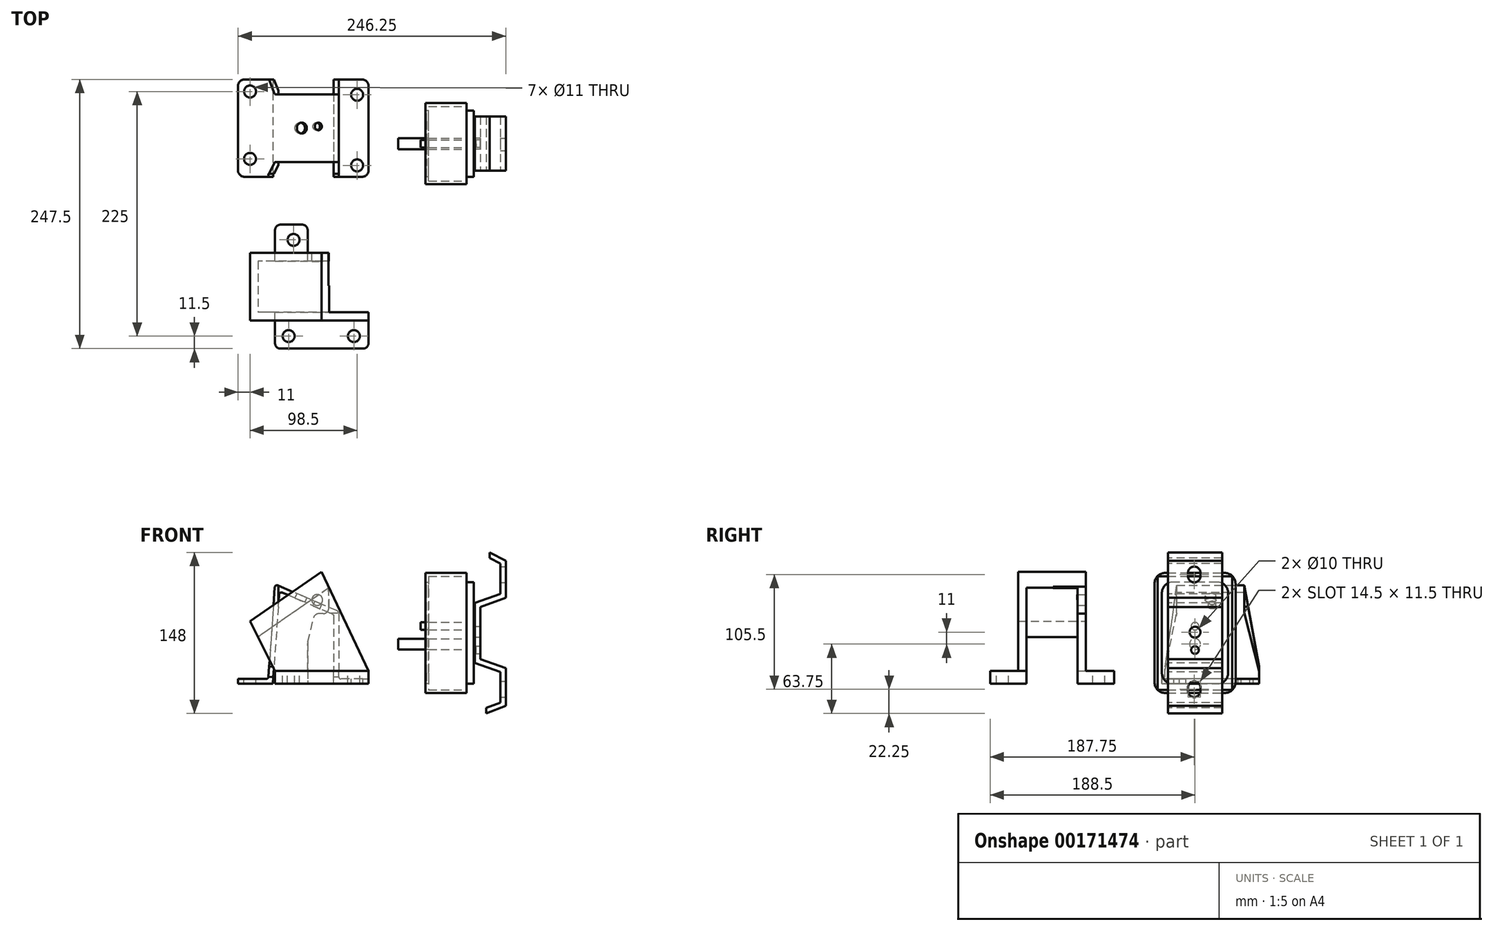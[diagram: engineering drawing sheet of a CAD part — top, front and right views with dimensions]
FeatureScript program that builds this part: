
annotation { "Feature Type Name" : "Feature", "Feature Type Description" : "" }
export const myFeature = defineFeature(function(context is Context, id is Id, definition is map)
    precondition{}
    {
        {
            var Q0;
            Q0=qCreatedBy(makeId("Front.planeOp"),FACE);
            var sketch = newSketch(context, id + "F0", { "sketchPlane" : qUnion([Q0])});
            skLineSegment(sketch, "E0", {"start": v(0, 0) * mm, "end": v(-120, 0) * mm});
            skPoint(sketch, "E1", {"position": v(-60, 0) * mm});
            skPoint(sketch, "E2", {"position": v(-32, 0) * mm});
            skPoint(sketch, "E3", {"position": v(-88, 0) * mm});
            skLineSegment(sketch, "E4", {"start": v(-32, 0) * mm, "end": v(-32, 63.5) * mm});
            skPoint(sketch, "E5", {"position": v(-82, 85) * mm});
            skLineSegment(sketch, "E6", {"start": v(-82, 85) * mm, "end": v(-88, 0) * mm});
            skLineSegment(sketch, "E7", {"start": v(-82, 85) * mm, "end": v(-32, 63.5) * mm});
            skLineSegment(sketch, "E8.0", {"start": v(-86.04, 91.64) * mm, "end": v(-92.49, 0.32) * mm});
            skLineSegment(sketch, "E8.1", {"start": v(-86.04, 91.64) * mm, "end": v(-27.5, 66.46) * mm});
            skLineSegment(sketch, "E8.2", {"start": v(-27.5, 0) * mm, "end": v(-27.5, 66.46) * mm});
            skLineSegment(sketch, "E9", {"start": v(-32, 0) * mm, "end": v(-27.5, 0) * mm});
            skPoint(sketch, "E10", {"position": v(-92.5, 0) * mm});
            skLineSegment(sketch, "E11", {"start": v(-92.5, 0) * mm, "end": v(-92.49, 0.32) * mm});
            skLineSegment(sketch, "E12", {"start": v(0, 0) * mm, "end": v(0, 4.5) * mm});
            skLineSegment(sketch, "E13", {"start": v(0, 4.5) * mm, "end": v(-27.5, 4.5) * mm});
            skLineSegment(sketch, "E14", {"start": v(-120, 0) * mm, "end": v(-120, 4.5) * mm});
            skLineSegment(sketch, "E15", {"start": v(-120, 4.5) * mm, "end": v(-92.2, 4.5) * mm});
            skSolve(sketch);
        }
        {
            var Q0;
            Q0=makeQuery(id+"F0.imprint","IMPRINT",FACE,{"disambiguationData":[TD([[makeQuery(id+"F0.imprint","IMPRINT",EDGE,{"derivedFrom":sQuery(id+"F0.wireOp",EDGE,"E4")}),-1.0]])]});
            var Q1;
            {var subQ0=sQuery(id+"F0.wireOp",EDGE,"E12");Q1=makeQuery(id+"F0.imprint","IMPRINT",FACE,{"disambiguationData":[TD([[makeQuery(id+"F0.imprint","IMPRINT",EDGE,{"derivedFrom":subQ0}),1.0]])]});}
            var Q2;
            {var subQ1=sQuery(id+"F0.wireOp",EDGE,"E11");Q2=makeQuery(id+"F0.imprint","IMPRINT",FACE,{"disambiguationData":[TD([[makeQuery(id+"F0.imprint","IMPRINT",EDGE,{"derivedFrom":subQ1}),1.0]])]});}
            extrude(context, id + "F1", {"entities" : qUnion([Q0, Q1, Q2]), "oppositeDirection" : true, "depth" : 89.5 * mm});
        }
        {
            var Q0;
            Q0=makeQuery(id+"F1.opExtrude","SWEPT_EDGE",EDGE,{"disambiguationData":[OSD([sQuery(id+"F0.wireOp",EDGE,"E8.0"),sQuery(id+"F0.wireOp",EDGE,"E8.1")])]});
            var Q1;
            Q1=makeQuery(id+"F1.opExtrude","SWEPT_EDGE",EDGE,{"disambiguationData":[OSD([sQuery(id+"F0.wireOp",EDGE,"E6"),sQuery(id+"F0.wireOp",EDGE,"E7")])]});
            var Q2;
            Q2=makeQuery(id+"F1.opExtrude","SWEPT_EDGE",EDGE,{"disambiguationData":[OSD([sQuery(id+"F0.wireOp",EDGE,"E4"),sQuery(id+"F0.wireOp",EDGE,"E7")])]});
            var Q3;
            Q3=makeQuery(id+"F1.opExtrude","SWEPT_EDGE",EDGE,{"disambiguationData":[OSD([sQuery(id+"F0.wireOp",EDGE,"E8.1"),sQuery(id+"F0.wireOp",EDGE,"E8.2")])]});
            var Q4;
            Q4=makeQuery(id+"F1.opExtrude","SWEPT_EDGE",EDGE,{"disambiguationData":[OSD([sQuery(id+"F0.wireOp",EDGE,"E8.0"),sQuery(id+"F0.wireOp",EDGE,"E15")])]});
            var Q5;
            Q5=makeQuery(id+"F1.opExtrude","SWEPT_EDGE",EDGE,{"disambiguationData":[OSD([sQuery(id+"F0.wireOp",EDGE,"E8.2"),sQuery(id+"F0.wireOp",EDGE,"E13")])]});
            fillet(context, id + "F2", {"entities" : qUnion([Q0, Q1, Q2, Q3, Q4, Q5]), "radius" : 2 * mm, "tangentPropagation" : true, "allowEdgeOverflow" : false});
        }
        {
            var Q0;
            Q0=makeQuery(id+"F1.opExtrude","SWEPT_FACE",FACE,{"disambiguationData":[OSD([sQuery(id+"F0.wireOp",EDGE,"E8.2")])]});
            var sketch = newSketch(context, id + "F3", { "sketchPlane" : qUnion([Q0])});
            skLineSegment(sketch, "E16.0", {"start": v(89.5, 90.52) * mm, "end": v(0, 90.52) * mm});
            skPoint(sketch, "E17", {"position": v(44.75, 90.52) * mm});
            skPoint(sketch, "E18", {"position": v(75.85, 90.52) * mm});
            skPoint(sketch, "E19", {"position": v(13.65, 90.52) * mm});
            skLineSegment(sketch, "E20.0", {"start": v(89.5, 65.15) * mm, "end": v(0, 65.15) * mm});
            skLineSegment(sketch, "E21.0", {"start": v(0, 6.5) * mm, "end": v(89.5, 6.5) * mm});
            skPoint(sketch, "E22", {"position": v(44.75, 6.5) * mm});
            skPoint(sketch, "E23", {"position": v(2.75, 6.5) * mm});
            skLineSegment(sketch, "E24", {"start": v(13.65, 90.52) * mm, "end": v(13.65, 65.15) * mm});
            skLineSegment(sketch, "E25", {"start": v(75.85, 90.52) * mm, "end": v(75.85, 65.15) * mm});
            skLineSegment(sketch, "E26.0", {"start": v(0, 6.5) * mm, "end": v(0, 65.15) * mm});
            skLineSegment(sketch, "E27.0", {"start": v(89.5, 6.5) * mm, "end": v(89.5, 65.15) * mm});
            skLineSegment(sketch, "E28.0", {"start": v(0, 90.52) * mm, "end": v(0, 66.98) * mm});
            skLineSegment(sketch, "E29.0", {"start": v(89.5, 90.52) * mm, "end": v(89.5, 66.98) * mm});
            skLineSegment(sketch, "E30", {"start": v(0, 66.98) * mm, "end": v(0, 65.15) * mm});
            skLineSegment(sketch, "E31", {"start": v(89.5, 66.98) * mm, "end": v(89.5, 65.15) * mm});
            skLineSegment(sketch, "E32", {"start": v(0, 90.52) * mm, "end": v(0, 93.52) * mm});
            skLineSegment(sketch, "E33", {"start": v(89.5, 6.5) * mm, "end": v(89.5, 11.5) * mm});
            skLineSegment(sketch, "E34", {"start": v(2.75, 6.5) * mm, "end": v(2.75, 11.5) * mm});
            skLineSegment(sketch, "E35", {"start": v(2.75, 11.5) * mm, "end": v(13.65, 65.15) * mm});
            skLineSegment(sketch, "E36", {"start": v(75.85, 65.15) * mm, "end": v(89.5, 11.5) * mm});
            skSolve(sketch);
        }
        {
            var Q0;
            {var subQ0=sQuery(id+"F3.wireOp",EDGE,"E25");Q0=makeQuery(id+"F3.imprint","IMPRINT",FACE,{"disambiguationData":[TD([[makeQuery(id+"F3.imprint","IMPRINT",EDGE,{"derivedFrom":subQ0}),1.0]])]});}
            var Q1;
            {var subQ0=sQuery(id+"F3.wireOp",EDGE,"E27.0");Q1=makeQuery(id+"F3.imprint","IMPRINT",FACE,{"disambiguationData":[TD([[makeQuery(id+"F3.imprint","IMPRINT",EDGE,{"derivedFrom":subQ0}),1.0]])]});}
            var Q2;
            {var subQ1=sQuery(id+"F3.wireOp",EDGE,"E26.0");Q2=makeQuery(id+"F3.imprint","IMPRINT",FACE,{"disambiguationData":[TD([[makeQuery(id+"F3.imprint","IMPRINT",EDGE,{"derivedFrom":subQ1}),-1.0]])]});}
            var Q3;
            {var subQ0=sQuery(id+"F3.wireOp",EDGE,"E24");Q3=makeQuery(id+"F3.imprint","IMPRINT",FACE,{"disambiguationData":[TD([[makeQuery(id+"F3.imprint","IMPRINT",EDGE,{"derivedFrom":subQ0}),-1.0]])]});}
            extrude(context, id + "F4", {"entities" : qUnion([Q0, Q1, Q2, Q3]), "operationType" : NewBodyOperationType.REMOVE, "oppositeDirection" : true, "depth" : 55.5 * mm});
        }
        {
            var Q0;
            Q0=makeQuery(id+"F4.boolean.opBoolean","COPY",EDGE,{"derivedFrom":makeQuery(id+"F4.opExtrude","SWEPT_EDGE",EDGE,{"disambiguationData":[OSD([sQuery(id+"F3.wireOp",EDGE,"E21.0"),sQuery(id+"F3.wireOp",EDGE,"E34")])]})});
            fillet(context, id + "F5", {"entities" : qUnion([Q0]), "radius" : 3 * mm, "tangentPropagation" : true, "allowEdgeOverflow" : false});
        }
        {
            var Q0;
            Q0=makeQuery(id+"F1.opExtrude","SWEPT_FACE",FACE,{"disambiguationData":[OSD([sQuery(id+"F0.wireOp",EDGE,"E8.0")])]});
            var sketch = newSketch(context, id + "F6", { "sketchPlane" : qUnion([Q0])});
            skLineSegment(sketch, "E37.0", {"start": v(-13.65, 84.26) * mm, "end": v(-13.65, 64.81) * mm});
            skLineSegment(sketch, "E38.0", {"start": v(-75.85, 84.26) * mm, "end": v(-75.85, 64.81) * mm});
            skLineSegment(sketch, "E39.1", {"start": v(-89.5, 4.55) * mm, "end": v(-89.5, 9.54) * mm});
            skLineSegment(sketch, "E40.0", {"start": v(-2.75, 7.53) * mm, "end": v(-2.75, 9.54) * mm});
            skLineSegment(sketch, "E41", {"start": v(-75.85, 84.26) * mm, "end": v(-89.5, 9.54) * mm});
            skLineSegment(sketch, "E42", {"start": v(-13.65, 84.26) * mm, "end": v(-2.75, 9.54) * mm});
            skLineSegment(sketch, "E43.0", {"start": v(-89.5, -0.14) * mm, "end": v(0, -0.14) * mm});
            skLineSegment(sketch, "E44", {"start": v(-2.75, 7.53) * mm, "end": v(-2.75, -0.14) * mm});
            skLineSegment(sketch, "E45.0", {"start": v(-89.5, 82.53) * mm, "end": v(-89.5, -0.14) * mm});
            skLineSegment(sketch, "E46.0", {"start": v(0, 82.53) * mm, "end": v(0, -0.14) * mm});
            skLineSegment(sketch, "E47.0", {"start": v(-89.5, 84.42) * mm, "end": v(0, 84.42) * mm});
            skLineSegment(sketch, "E48.0", {"start": v(-89.5, 82.53) * mm, "end": v(-89.5, 84.53) * mm});
            skLineSegment(sketch, "E49.0", {"start": v(0, 84.53) * mm, "end": v(0, 82.53) * mm});
            skLineSegment(sketch, "E50", {"start": v(-89.5, 84.42) * mm, "end": v(-89.5, 87.42) * mm});
            skLineSegment(sketch, "E51", {"start": v(-89.5, 87.42) * mm, "end": v(0, 87.42) * mm});
            skLineSegment(sketch, "E52", {"start": v(0, 87.42) * mm, "end": v(0, 84.42) * mm});
            skLineSegment(sketch, "E53", {"start": v(-13.65, 84.26) * mm, "end": v(-13.65, 87.42) * mm});
            skLineSegment(sketch, "E54", {"start": v(-75.85, 84.26) * mm, "end": v(-75.85, 87.42) * mm});
            skSolve(sketch);
        }
        {
            var Q0;
            {var subQ0=sQuery(id+"F6.wireOp",EDGE,"E45.0");var subQ1=sQuery(id+"F6.wireOp",EDGE,"E41");var subQ2=makeQuery(id+"F6.imprint","INTERSECT",VERTEX,{"derivedFrom":[subQ1,subQ0]});Q0=makeQuery(id+"F6.imprint","IMPRINT",FACE,{"disambiguationData":[TD([[makeQuery(id+"F6.imprint","IMPRINT",EDGE,{"disambiguationData":[TD([[subQ2,1.0]])],"derivedFrom":subQ1}),-1.0]])]});}
            var Q1;
            {var subQ0=sQuery(id+"F6.wireOp",EDGE,"E50");var subQ5=sQuery(id+"F6.wireOp",EDGE,"E51");var subQ6=makeQuery(id+"F6.imprint","INTERSECT",VERTEX,{"derivedFrom":[subQ0,subQ5]});Q1=makeQuery(id+"F6.imprint","IMPRINT",FACE,{"disambiguationData":[TD([[makeQuery(id+"F6.imprint","IMPRINT",EDGE,{"disambiguationData":[TD([[subQ6,-1.0]])],"derivedFrom":subQ5}),-1.0]])]});}
            var Q2;
            {var subQ8=sQuery(id+"F6.wireOp",EDGE,"E48.0");Q2=makeQuery(id+"F6.imprint","IMPRINT",FACE,{"disambiguationData":[TD([[makeQuery(id+"F6.imprint","IMPRINT",EDGE,{"derivedFrom":subQ8}),-1.0]])]});}
            var Q3;
            {var subQ0=sQuery(id+"F6.wireOp",EDGE,"E52");var subQ5=sQuery(id+"F6.wireOp",EDGE,"E51");var subQ6=makeQuery(id+"F6.imprint","INTERSECT",VERTEX,{"derivedFrom":[subQ5,subQ0]});Q3=makeQuery(id+"F6.imprint","IMPRINT",FACE,{"disambiguationData":[TD([[makeQuery(id+"F6.imprint","IMPRINT",EDGE,{"disambiguationData":[TD([[subQ6,1.0]])],"derivedFrom":subQ5}),-1.0]])]});}
            var Q4;
            {var subQ5=sQuery(id+"F6.wireOp",EDGE,"E49.0");Q4=makeQuery(id+"F6.imprint","IMPRINT",FACE,{"disambiguationData":[TD([[makeQuery(id+"F6.imprint","IMPRINT",EDGE,{"derivedFrom":subQ5}),-1.0]])]});}
            var Q5;
            {var subQ4=sQuery(id+"F6.wireOp",EDGE,"E40.0");Q5=makeQuery(id+"F6.imprint","IMPRINT",FACE,{"disambiguationData":[TD([[makeQuery(id+"F6.imprint","IMPRINT",EDGE,{"derivedFrom":subQ4}),-1.0]])]});}
            extrude(context, id + "F7", {"entities" : qUnion([Q0, Q1, Q2, Q3, Q4, Q5]), "operationType" : NewBodyOperationType.REMOVE, "oppositeDirection" : true, "depth" : 25 * mm});
        }
        {
            var Q0;
            Q0=makeQuery(id+"F1.opExtrude","SWEPT_FACE",FACE,{"disambiguationData":[OSD([sQuery(id+"F0.wireOp",EDGE,"E13")])]});
            var sketch = newSketch(context, id + "F8", { "sketchPlane" : qUnion([Q0])});
            skPoint(sketch, "E55", {"position": v(-10.5, 75.5) * mm});
            skPoint(sketch, "E56", {"position": v(-10.5, 10.5) * mm});
            skCircle(sketch, "E57", {"center": v(-10.5, 10.5) * mm, "radius": 5.5 * mm});
            skCircle(sketch, "E58", {"center": v(-10.5, 75.5) * mm, "radius": 5.5 * mm});
            skSolve(sketch);
        }
        {
            var Q0;
            Q0 = qSketchRegion(id + "F8", true);
            extrude(context, id + "F9", {"entities" : qUnion([Q0]), "operationType" : NewBodyOperationType.REMOVE, "oppositeDirection" : true, "depth" : 5 * mm});
        }
        {
            var Q0;
            Q0=makeQuery(id+"F1.opExtrude","SWEPT_FACE",FACE,{"disambiguationData":[OSD([sQuery(id+"F0.wireOp",EDGE,"E15")])]});
            var sketch = newSketch(context, id + "F10", { "sketchPlane" : qUnion([Q0])});
            skPoint(sketch, "E59", {"position": v(-109, 78.5) * mm});
            skPoint(sketch, "E60", {"position": v(-109, 16.5) * mm});
            skCircle(sketch, "E61", {"center": v(-109, 16.5) * mm, "radius": 5.5 * mm});
            skCircle(sketch, "E62", {"center": v(-109, 78.5) * mm, "radius": 5.5 * mm});
            skSolve(sketch);
        }
        {
            var Q0;
            Q0 = qSketchRegion(id + "F10", true);
            extrude(context, id + "F11", {"entities" : qUnion([Q0]), "operationType" : NewBodyOperationType.REMOVE, "oppositeDirection" : true, "depth" : 5 * mm});
        }
        {
            var Q0;
            Q0=makeQuery(id+"F1.opExtrude","SWEPT_FACE",FACE,{"disambiguationData":[OSD([sQuery(id+"F0.wireOp",EDGE,"E8.1")])]});
            var sketch = newSketch(context, id + "F12", { "sketchPlane" : qUnion([Q0])});
            skPoint(sketch, "E63", {"position": v(-88.32, 44.85) * mm});
            skCircle(sketch, "E64", {"center": v(-88.32, 44.85) * mm, "radius": 5 * mm});
            skPoint(sketch, "E65", {"position": v(-71.82, 46.35) * mm});
            skCircle(sketch, "E66", {"center": v(-71.82, 46.35) * mm, "radius": 3.5 * mm});
            skSolve(sketch);
        }
        {
            var Q0;
            Q0 = qSketchRegion(id + "F12", true);
            extrude(context, id + "F13", {"entities" : qUnion([Q0]), "operationType" : NewBodyOperationType.REMOVE, "oppositeDirection" : true, "depth" : 5 * mm});
        }
        {
            var Q0;
            Q0=makeQuery(id+"F1.opExtrude","CAP_EDGE",EDGE,{"disambiguationData":[OSD([sQuery(id+"F0.wireOp",EDGE,"E12")])],"isStart":false});
            var Q1;
            Q1=makeQuery(id+"F1.opExtrude","CAP_EDGE",EDGE,{"disambiguationData":[OSD([sQuery(id+"F0.wireOp",EDGE,"E12")])],"isStart":true});
            var Q2;
            Q2=makeQuery(id+"F1.opExtrude","CAP_EDGE",EDGE,{"disambiguationData":[OSD([sQuery(id+"F0.wireOp",EDGE,"E14")])],"isStart":true});
            var Q3;
            Q3=makeQuery(id+"F1.opExtrude","CAP_EDGE",EDGE,{"disambiguationData":[OSD([sQuery(id+"F0.wireOp",EDGE,"E14")])],"isStart":false});
            fillet(context, id + "F14", {"entities" : qUnion([Q0, Q1, Q2, Q3]), "radius" : 6 * mm, "tangentPropagation" : true, "allowEdgeOverflow" : false});
        }
        {
            var Q0;
            Q0=qCreatedBy(makeId("Front.planeOp"),FACE);
            var sketch = newSketch(context, id + "F15", { "sketchPlane" : qUnion([Q0])});
            skPoint(sketch, "E67", {"position": v(75, 0) * mm});
            skLineSegment(sketch, "E68", {"start": v(75, 0) * mm, "end": v(96.75, 0) * mm});
            skLineSegment(sketch, "E69", {"start": v(75, 0) * mm, "end": v(53.25, 0) * mm});
            skLineSegment(sketch, "E70", {"start": v(53.25, 0) * mm, "end": v(53.25, 93.5) * mm});
            skLineSegment(sketch, "E71", {"start": v(53.25, 93.5) * mm, "end": v(96.75, 93.5) * mm});
            skLineSegment(sketch, "E72", {"start": v(96.75, 93.5) * mm, "end": v(96.75, 0) * mm});
            skSolve(sketch);
        }
        {
            var Q0;
            Q0 = qSketchRegion(id + "F15", true);
            extrude(context, id + "F16", {"entities" : qUnion([Q0]), "oppositeDirection" : true, "depth" : 61 * mm});
        }
        {
            var Q0;
            Q0=makeQuery(id+"F16.opExtrude","SWEPT_FACE",FACE,{"disambiguationData":[OSD([sQuery(id+"F15.wireOp",EDGE,"E72")])]});
            var sketch = newSketch(context, id + "F17", { "sketchPlane" : qUnion([Q0])});
            skPoint(sketch, "E73", {"position": v(30.5, 47.5) * mm});
            skCircle(sketch, "E74", {"center": v(30.5, 47.5) * mm, "radius": 5 * mm});
            skPoint(sketch, "E75", {"position": v(30.5, 31) * mm});
            skCircle(sketch, "E76", {"center": v(30.5, 31) * mm, "radius": 3.5 * mm});
            skSolve(sketch);
        }
        {
            var Q0;
            Q0=makeQuery(id+"F17.imprint","IMPRINT",FACE,{"disambiguationData":[TD([[makeQuery(id+"F17.imprint","IMPRINT",EDGE,{"derivedFrom":sQuery(id+"F17.wireOp",EDGE,"E74")}),1.0]])]});
            extrude(context, id + "F18", {"entities" : qUnion([Q0]), "operationType" : NewBodyOperationType.ADD, "depth" : 20 * mm});
        }
        {
            var Q0;
            Q0 = qSketchRegion(id + "F17", true);
            extrude(context, id + "F19", {"entities" : qUnion([Q0]), "operationType" : NewBodyOperationType.ADD, "depth" : 2.25 * mm});
        }
        {
            var Q0;
            Q0=makeQuery(id+"F16.opExtrude","SWEPT_FACE",FACE,{"disambiguationData":[OSD([sQuery(id+"F15.wireOp",EDGE,"E70")])]});
            var sketch = newSketch(context, id + "F20", { "sketchPlane" : qUnion([Q0])});
            skPoint(sketch, "E77", {"position": v(-30.5, 36.5) * mm});
            skPoint(sketch, "E78", {"position": v(-30.5, 53) * mm});
            skCircle(sketch, "E79", {"center": v(-30.5, 36.5) * mm, "radius": 5 * mm});
            skCircle(sketch, "E80", {"center": v(-30.5, 53) * mm, "radius": 3.5 * mm});
            skSolve(sketch);
        }
        {
            var Q0;
            Q0=makeQuery(id+"F20.imprint","IMPRINT",FACE,{"disambiguationData":[TD([[makeQuery(id+"F20.imprint","IMPRINT",EDGE,{"derivedFrom":sQuery(id+"F20.wireOp",EDGE,"E79")}),1.0]])]});
            extrude(context, id + "F21", {"entities" : qUnion([Q0]), "operationType" : NewBodyOperationType.ADD, "depth" : 26 * mm});
        }
        {
            var Q0;
            Q0 = qSketchRegion(id + "F20", true);
            extrude(context, id + "F22", {"entities" : qUnion([Q0]), "operationType" : NewBodyOperationType.ADD, "depth" : 5.5 * mm});
        }
        {
            var Q0;
            Q0=makeQuery(id+"F16.opExtrude","CAP_EDGE",EDGE,{"disambiguationData":[OSD([sQuery(id+"F15.wireOp",EDGE,"E71")])],"isStart":true});
            var Q1;
            Q1=makeQuery(id+"F16.opExtrude","CAP_EDGE",EDGE,{"disambiguationData":[OSD([sQuery(id+"F15.wireOp",EDGE,"E71")])],"isStart":false});
            var Q2;
            Q2=makeQuery(id+"F16.opExtrude","CAP_EDGE",EDGE,{"disambiguationData":[OSD([sQuery(id+"F15.wireOp",EDGE,"E68"),sQuery(id+"F15.wireOp",EDGE,"E69")])],"isStart":false});
            var Q3;
            Q3=makeQuery(id+"F16.opExtrude","CAP_EDGE",EDGE,{"disambiguationData":[OSD([sQuery(id+"F15.wireOp",EDGE,"E68"),sQuery(id+"F15.wireOp",EDGE,"E69")])],"isStart":true});
            fillet(context, id + "F23", {"entities" : qUnion([Q0, Q1, Q2, Q3]), "radius" : 10 * mm, "tangentPropagation" : true, "allowEdgeOverflow" : false});
        }
        {
            var Q0;
            Q0=makeQuery(id+"F16.opExtrude","SWEPT_FACE",FACE,{"disambiguationData":[OSD([sQuery(id+"F15.wireOp",EDGE,"E70")])]});
            cPlane(context, id + "F24", {"entities" : qUnion([Q0]), "cplaneType" : CPlaneType.OFFSET, "offset" : 1 * mm, "width" : 150 * mm, "height" : 150 * mm});
        }
        {
            var Q0;
            Q0=qCreatedBy(id+"F24.planeOp",FACE);
            var sketch = newSketch(context, id + "F25", { "sketchPlane" : qUnion([Q0])});
            skLineSegment(sketch, "E81.0", {"start": v(-51, 93.5) * mm, "end": v(-10, 93.5) * mm});
            skLineSegment(sketch, "E82.0", {"start": v(-61, 10) * mm, "end": v(-61, 83.5) * mm});
            skPoint(sketch, "E83", {"position": v(-30.5, 46.75) * mm});
            skPoint(sketch, "E83.positionSnap0", {"position": v(-61, 46.75) * mm});
            skPoint(sketch, "E83.positionSnap1", {"position": v(-30.5, 93.5) * mm});
            skLineSegment(sketch, "E84.bottom", {"start": v(6.75, 102) * mm, "end": v(-67.75, 102) * mm});
            skLineSegment(sketch, "E84.top", {"start": v(6.75, -8.5) * mm, "end": v(-67.75, -8.5) * mm});
            skLineSegment(sketch, "E84.left", {"start": v(6.75, 102) * mm, "end": v(6.75, -8.5) * mm});
            skLineSegment(sketch, "E84.right", {"start": v(-67.75, 102) * mm, "end": v(-67.75, -8.5) * mm});
            skCircle(sketch, "E85.0", {"center": v(-30.5, 36.5) * mm, "radius": 5 * mm});
            skCircle(sketch, "E86.0", {"center": v(-30.5, 53) * mm, "radius": 3.5 * mm});
            skSolve(sketch);
        }
        {
            var Q0;
            Q0 = qSketchRegion(id + "F25", true);
            extrude(context, id + "F26", {"entities" : qUnion([Q0]), "oppositeDirection" : true, "depth" : 38 * mm});
        }
        {
            var Q0;
            Q0=makeQuery(id+"F26.opExtrude","CAP_FACE",FACE,{"disambiguationData":[OSD([sQuery(id+"F25.wireOp",EDGE,"E84.bottom"),sQuery(id+"F25.wireOp",EDGE,"E84.top"),sQuery(id+"F25.wireOp",EDGE,"E84.left"),sQuery(id+"F25.wireOp",EDGE,"E84.right")])],"isStart":false});
            var sketch = newSketch(context, id + "F27", { "sketchPlane" : qUnion([Q0])});
            skLineSegment(sketch, "E87.0", {"start": v(-6.75, 102) * mm, "end": v(67.75, 102) * mm});
            skLineSegment(sketch, "E88.0", {"start": v(-6.75, 102) * mm, "end": v(-6.75, -8.5) * mm});
            skLineSegment(sketch, "E89.0", {"start": v(67.75, 102) * mm, "end": v(67.75, -8.5) * mm});
            skLineSegment(sketch, "E90.0", {"start": v(-6.75, -8.5) * mm, "end": v(67.75, -8.5) * mm});
            skLineSegment(sketch, "E91.0", {"start": v(-3.75, 99) * mm, "end": v(64.75, 99) * mm});
            skLineSegment(sketch, "E91.1", {"start": v(-3.75, 99) * mm, "end": v(-3.75, -5.5) * mm});
            skLineSegment(sketch, "E91.2", {"start": v(-3.75, -5.5) * mm, "end": v(64.75, -5.5) * mm});
            skLineSegment(sketch, "E91.3", {"start": v(64.75, 99) * mm, "end": v(64.75, -5.5) * mm});
            skSolve(sketch);
        }
        {
            var Q0;
            Q0=makeQuery(id+"F27.imprint","IMPRINT",FACE,{"disambiguationData":[TD([[makeQuery(id+"F27.imprint","IMPRINT",EDGE,{"derivedFrom":sQuery(id+"F27.wireOp",EDGE,"E91.0")}),-1.0]])]});
            extrude(context, id + "F28", {"entities" : qUnion([Q0]), "operationType" : NewBodyOperationType.REMOVE, "oppositeDirection" : true, "depth" : 35 * mm});
        }
        {
            var Q0;
            Q0=makeQuery(id+"F26.opExtrude","SWEPT_EDGE",EDGE,{"disambiguationData":[OSD([sQuery(id+"F25.wireOp",EDGE,"E84.bottom"),sQuery(id+"F25.wireOp",EDGE,"E84.left")])]});
            var Q1;
            Q1=makeQuery(id+"F26.opExtrude","SWEPT_EDGE",EDGE,{"disambiguationData":[OSD([sQuery(id+"F25.wireOp",EDGE,"E84.bottom"),sQuery(id+"F25.wireOp",EDGE,"E84.right")])]});
            var Q2;
            Q2=makeQuery(id+"F26.opExtrude","SWEPT_EDGE",EDGE,{"disambiguationData":[OSD([sQuery(id+"F25.wireOp",EDGE,"E84.top"),sQuery(id+"F25.wireOp",EDGE,"E84.right")])]});
            var Q3;
            Q3=makeQuery(id+"F26.opExtrude","SWEPT_EDGE",EDGE,{"disambiguationData":[OSD([sQuery(id+"F25.wireOp",EDGE,"E84.top"),sQuery(id+"F25.wireOp",EDGE,"E84.left")])]});
            fillet(context, id + "F29", {"entities" : qUnion([Q0, Q1, Q2, Q3]), "radius" : 10 * mm, "tangentPropagation" : true, "allowEdgeOverflow" : false});
        }
        {
            var Q0;
            Q0=makeQuery(id+"F16.opExtrude","SWEPT_FACE",FACE,{"disambiguationData":[OSD([sQuery(id+"F15.wireOp",EDGE,"E72")])]});
            cPlane(context, id + "F30", {"entities" : qUnion([Q0]), "cplaneType" : CPlaneType.OFFSET, "offset" : 1 * mm, "width" : 150 * mm, "height" : 150 * mm});
        }
        {
            var Q0;
            Q0=qCreatedBy(id+"F30.planeOp",FACE);
            var sketch = newSketch(context, id + "F31", { "sketchPlane" : qUnion([Q0])});
            skLineSegment(sketch, "E92.0", {"start": v(61, 83.5) * mm, "end": v(61, 10) * mm});
            skLineSegment(sketch, "E93.0", {"start": v(51, 0) * mm, "end": v(10, 0) * mm});
            skPoint(sketch, "E94", {"position": v(30.5, 46.75) * mm});
            skPoint(sketch, "E94.positionSnap0", {"position": v(30.5, 0) * mm});
            skPoint(sketch, "E94.positionSnap1", {"position": v(61, 46.75) * mm});
            skLineSegment(sketch, "E95.bottom", {"start": v(55.5, -27.25) * mm, "end": v(5.5, -27.25) * mm});
            skLineSegment(sketch, "E95.top", {"start": v(55.5, 120.75) * mm, "end": v(5.5, 120.75) * mm});
            skLineSegment(sketch, "E95.left", {"start": v(55.5, -27.25) * mm, "end": v(55.5, 120.75) * mm});
            skLineSegment(sketch, "E95.right", {"start": v(5.5, -27.25) * mm, "end": v(5.5, 120.75) * mm});
            skCircle(sketch, "E96.0.0", {"center": v(30.5, 31) * mm, "radius": 3.5 * mm});
            skCircle(sketch, "E97.0", {"center": v(30.5, 47.5) * mm, "radius": 5 * mm});
            skSolve(sketch);
        }
        {
            var Q0;
            Q0 = qSketchRegion(id + "F31", true);
            extrude(context, id + "F32", {"entities" : qUnion([Q0]), "depth" : 28.5 * mm});
        }
        {
            var Q0;
            Q0=makeQuery(id+"F32.opExtrude","SWEPT_FACE",FACE,{"disambiguationData":[OSD([sQuery(id+"F31.wireOp",EDGE,"E95.right")])]});
            var sketch = newSketch(context, id + "F33", { "sketchPlane" : qUnion([Q0])});
            skLineSegment(sketch, "E98.0", {"start": v(126.25, -27.25) * mm, "end": v(126.25, 120.75) * mm});
            skPoint(sketch, "E99", {"position": v(97.75, 46.75) * mm});
            skPoint(sketch, "E100", {"position": v(97.75, 74.25) * mm});
            skPoint(sketch, "E101", {"position": v(97.75, 19.25) * mm});
            skPoint(sketch, "E102", {"position": v(121.25, -27.25) * mm});
            skLineSegment(sketch, "E103", {"start": v(121.25, -27.25) * mm, "end": v(121.25, 120.75) * mm, "construction": true});
            skPoint(sketch, "E104", {"position": v(121.25, 46.75) * mm});
            skPoint(sketch, "E105", {"position": v(121.25, 82.75) * mm});
            skPoint(sketch, "E106", {"position": v(121.25, 10.75) * mm});
            skPoint(sketch, "E107", {"position": v(121.25, -17.25) * mm});
            skPoint(sketch, "E108", {"position": v(121.25, 110.75) * mm});
            skLineSegment(sketch, "E109", {"start": v(97.75, 19.25) * mm, "end": v(121.25, 10.75) * mm});
            skLineSegment(sketch, "E110", {"start": v(121.25, 10.75) * mm, "end": v(121.25, -17.25) * mm});
            skLineSegment(sketch, "E111", {"start": v(97.75, 19.25) * mm, "end": v(97.75, 74.25) * mm});
            skLineSegment(sketch, "E112", {"start": v(97.75, 74.25) * mm, "end": v(121.25, 82.75) * mm});
            skLineSegment(sketch, "E113", {"start": v(121.25, 82.75) * mm, "end": v(121.25, 110.75) * mm});
            skPoint(sketch, "E114", {"position": v(111.25, 120.75) * mm});
            skPoint(sketch, "E115", {"position": v(108.25, -27.25) * mm});
            skLineSegment(sketch, "E116", {"start": v(108.25, -27.25) * mm, "end": v(108.25, -22.25) * mm});
            skLineSegment(sketch, "E117", {"start": v(108.25, -22.25) * mm, "end": v(121.25, -17.25) * mm});
            skLineSegment(sketch, "E118", {"start": v(111.25, 120.75) * mm, "end": v(111.25, 115.75) * mm});
            skLineSegment(sketch, "E119", {"start": v(111.25, 115.75) * mm, "end": v(121.25, 110.75) * mm});
            skLineSegment(sketch, "E120.1", {"start": v(102.75, 22.76) * mm, "end": v(102.75, 70.74) * mm});
            skLineSegment(sketch, "E121", {"start": v(108.25, -27.25) * mm, "end": v(126.25, -20.33) * mm});
            skLineSegment(sketch, "E122", {"start": v(111.25, 120.75) * mm, "end": v(126.25, 113.25) * mm});
            skLineSegment(sketch, "E123", {"start": v(126.25, 113.25) * mm, "end": v(126.25, -20.33) * mm});
            skLineSegment(sketch, "E124", {"start": v(102.75, 22.76) * mm, "end": v(126.25, 14.26) * mm});
            skLineSegment(sketch, "E125", {"start": v(102.75, 70.74) * mm, "end": v(126.25, 79.24) * mm});
            skLineSegment(sketch, "E126.0", {"start": v(126.25, 120.75) * mm, "end": v(97.75, 120.75) * mm});
            skLineSegment(sketch, "E127.0", {"start": v(97.75, -27.25) * mm, "end": v(97.75, 120.75) * mm});
            skLineSegment(sketch, "E128.0", {"start": v(126.25, -27.25) * mm, "end": v(97.75, -27.25) * mm});
            skSolve(sketch);
        }
        {
            var Q0;
            {var subQ3=sQuery(id+"F33.wireOp",EDGE,"E122");Q0=makeQuery(id+"F33.imprint","IMPRINT",FACE,{"disambiguationData":[TD([[makeQuery(id+"F33.imprint","IMPRINT",EDGE,{"derivedFrom":subQ3}),1.0]])]});}
            var Q1;
            {var subQ4=sQuery(id+"F33.wireOp",EDGE,"E112");Q1=makeQuery(id+"F33.imprint","IMPRINT",FACE,{"disambiguationData":[TD([[makeQuery(id+"F33.imprint","IMPRINT",EDGE,{"derivedFrom":subQ4}),1.0]])]});}
            var Q2;
            Q2=makeQuery(id+"F33.imprint","IMPRINT",FACE,{"disambiguationData":[TD([[makeQuery(id+"F33.imprint","IMPRINT",EDGE,{"derivedFrom":sQuery(id+"F33.wireOp",EDGE,"E120.1")}),-1.0]])]});
            var Q3;
            {var subQ1=sQuery(id+"F33.wireOp",EDGE,"E109");Q3=makeQuery(id+"F33.imprint","IMPRINT",FACE,{"disambiguationData":[TD([[makeQuery(id+"F33.imprint","IMPRINT",EDGE,{"derivedFrom":subQ1}),-1.0]])]});}
            var Q4;
            {var subQ3=sQuery(id+"F33.wireOp",EDGE,"E121");Q4=makeQuery(id+"F33.imprint","IMPRINT",FACE,{"disambiguationData":[TD([[makeQuery(id+"F33.imprint","IMPRINT",EDGE,{"derivedFrom":subQ3}),-1.0]])]});}
            extrude(context, id + "F34", {"entities" : qUnion([Q0, Q1, Q2, Q3, Q4]), "operationType" : NewBodyOperationType.REMOVE, "oppositeDirection" : true, "depth" : 50 * mm});
        }
        {
            var Q0;
            {var subQ0=sQuery(id+"F31.wireOp",EDGE,"E95.left");var subQ1=sQuery(id+"F31.wireOp",EDGE,"E95.right");Q0=makeQuery(id+"F34.boolean.opBoolean","SPLIT",FACE,{"disambiguationData":[TD([makeQuery(id+"F34.opExtrude","SWEPT_FACE",FACE,{"disambiguationData":[OSD([sQuery(id+"F33.wireOp",EDGE,"E122")])]})])],"derivedFrom":makeQuery(id+"F32.opExtrude","CAP_FACE",FACE,{"disambiguationData":[OSD([sQuery(id+"F31.wireOp",EDGE,"E95.bottom"),sQuery(id+"F31.wireOp",EDGE,"E95.top"),subQ0,subQ1,sQuery(id+"F31.wireOp",EDGE,"E96.0.0"),sQuery(id+"F31.wireOp",EDGE,"E97.0")])],"isStart":false})});}
            var sketch = newSketch(context, id + "F35", { "sketchPlane" : qUnion([Q0])});
            skPoint(sketch, "E129", {"position": v(35.5, -12.25) * mm});
            skLineSegment(sketch, "E130.bottom", {"start": v(29.75, -12.25) * mm, "end": v(29.75, -12.25) * mm});
            skLineSegment(sketch, "E130.top", {"start": v(29.75, 2.25) * mm, "end": v(29.75, 2.25) * mm});
            skLineSegment(sketch, "E130.left", {"start": v(35.5, -6.5) * mm, "end": v(35.5, -3.5) * mm});
            skLineSegment(sketch, "E130.right", {"start": v(24, -6.5) * mm, "end": v(24, -3.5) * mm});
            skPoint(sketch, "E131.visualSharp", {"position": v(24, -12.25) * mm});
            skArc(sketch, "E131.filletArc", {"start": v(24, -6.5) * mm, "mid": v(25.68, -10.57) * mm, "end": v(29.75, -12.25) * mm});
            skArc(sketch, "E132.filletArc", {"start": v(29.75, -12.25) * mm, "mid": v(33.82, -10.57) * mm, "end": v(35.5, -6.5) * mm});
            skPoint(sketch, "E133.visualSharp", {"position": v(24, 2.25) * mm});
            skArc(sketch, "E133.filletArc", {"start": v(29.75, 2.25) * mm, "mid": v(25.68, 0.57) * mm, "end": v(24, -3.5) * mm});
            skPoint(sketch, "E134.visualSharp", {"position": v(35.5, 2.25) * mm});
            skArc(sketch, "E134.filletArc", {"start": v(35.5, -3.5) * mm, "mid": v(33.82, 0.57) * mm, "end": v(29.75, 2.25) * mm});
            skPoint(sketch, "E135.endSnap0", {"position": v(5.5, 46.75) * mm});
            skLineSegment(sketch, "E136", {"start": v(29.75, 2.25) * mm, "end": v(29.75, 93.25) * mm});
            skLineSegment(sketch, "E137", {"start": v(29.75, 47.75) * mm, "end": v(39.75, 47.75) * mm});
            skPoint(sketch, "E137.endSnap0", {"position": v(29.75, 47.75) * mm});
            skArc(sketch, "E138.MirrorCS", {"start": v(29.75, 93.25) * mm, "mid": v(25.68, 94.93) * mm, "end": v(24, 99) * mm});
            skArc(sketch, "E139.MirrorCS", {"start": v(35.5, 99) * mm, "mid": v(33.82, 94.93) * mm, "end": v(29.75, 93.25) * mm});
            skLineSegment(sketch, "E140.MirrorCS", {"start": v(35.5, 102) * mm, "end": v(35.5, 99) * mm});
            skArc(sketch, "E141.MirrorCS", {"start": v(29.75, 107.75) * mm, "mid": v(33.82, 106.07) * mm, "end": v(35.5, 102) * mm});
            skArc(sketch, "E142.MirrorCS", {"start": v(24, 102) * mm, "mid": v(25.68, 106.07) * mm, "end": v(29.75, 107.75) * mm});
            skLineSegment(sketch, "E143.MirrorCS", {"start": v(24, 102) * mm, "end": v(24, 99) * mm});
            skSolve(sketch);
        }
        {
            var Q0;
            Q0 = qSketchRegion(id + "F35", true);
            extrude(context, id + "F36", {"entities" : qUnion([Q0]), "operationType" : NewBodyOperationType.REMOVE, "oppositeDirection" : true, "depth" : 5 * mm});
        }
        {
            var Q0;
            Q0=qCreatedBy(makeId("Front.planeOp"),FACE);
            cPlane(context, id + "F37", {"entities" : qUnion([Q0]), "cplaneType" : CPlaneType.OFFSET, "offset" : 70 * mm, "width" : 150 * mm, "height" : 150 * mm});
        }
        {
            var Q0;
            Q0=qCreatedBy(id+"F37.planeOp",FACE);
            var sketch = newSketch(context, id + "F38", { "sketchPlane" : qUnion([Q0])});
            skLineSegment(sketch, "E144", {"start": v(0, 0) * mm, "end": v(-86, 0) * mm});
            skLineSegment(sketch, "E145", {"start": v(-86, 0) * mm, "end": v(-86, 12) * mm});
            skLineSegment(sketch, "E146", {"start": v(-86, 12) * mm, "end": v(0, 12) * mm});
            skLineSegment(sketch, "E147", {"start": v(0, 12) * mm, "end": v(0, 0) * mm});
            skPoint(sketch, "E148", {"position": v(-109, 57.5) * mm});
            skLineSegment(sketch, "E149", {"start": v(-109, 57.5) * mm, "end": v(-43.2, 103) * mm});
            skLineSegment(sketch, "E150", {"start": v(-43.2, 103) * mm, "end": v(0, 12) * mm});
            skLineSegment(sketch, "E151", {"start": v(-109, 57.5) * mm, "end": v(-86, 12) * mm});
            skSolve(sketch);
        }
        {
            var Q0;
            Q0 = qSketchRegion(id + "F38", true);
            extrude(context, id + "F39", {"entities" : qUnion([Q0]), "depth" : 62 * mm});
        }
        {
            var Q0;
            Q0=makeQuery(id+"F39.opExtrude","SWEPT_FACE",FACE,{"disambiguationData":[OSD([sQuery(id+"F38.wireOp",EDGE,"E149")])]});
            cPlane(context, id + "F40", {"entities" : qUnion([Q0]), "cplaneType" : CPlaneType.OFFSET, "offset" : 16 * mm, "oppositeDirection" : true, "width" : 150 * mm, "height" : 150 * mm});
        }
        {
            var Q0;
            Q0=qCreatedBy(id+"F40.planeOp",FACE);
            var sketch = newSketch(context, id + "F41", { "sketchPlane" : qUnion([Q0])});
            skLineSegment(sketch, "E152.0", {"start": v(23.05, -132) * mm, "end": v(23.05, -70) * mm});
            skLineSegment(sketch, "E153.0", {"start": v(-56.95, -132) * mm, "end": v(23.05, -132) * mm});
            skLineSegment(sketch, "E154.0", {"start": v(-56.95, -132) * mm, "end": v(-56.95, -70) * mm});
            skLineSegment(sketch, "E155.0", {"start": v(-56.95, -70) * mm, "end": v(23.05, -70) * mm});
            skPoint(sketch, "E156", {"position": v(23.05, -77.5) * mm});
            skPoint(sketch, "E157", {"position": v(23.05, -124.5) * mm});
            skLineSegment(sketch, "E158", {"start": v(23.05, -77.5) * mm, "end": v(-56.95, -77.5) * mm});
            skLineSegment(sketch, "E159", {"start": v(23.05, -124.5) * mm, "end": v(-56.95, -124.5) * mm});
            skLineSegment(sketch, "E160", {"start": v(-56.95, -77.5) * mm, "end": v(-71.95, -77.5) * mm});
            skLineSegment(sketch, "E161", {"start": v(-71.95, -77.5) * mm, "end": v(-71.95, -124.5) * mm});
            skLineSegment(sketch, "E162", {"start": v(-71.95, -124.5) * mm, "end": v(-56.95, -124.5) * mm});
            skSolve(sketch);
        }
        {
            var Q0;
            {var subQ0=sQuery(id+"F41.wireOp",EDGE,"E158");Q0=makeQuery(id+"F41.imprint","IMPRINT",FACE,{"disambiguationData":[TD([[makeQuery(id+"F41.imprint","IMPRINT",EDGE,{"derivedFrom":subQ0}),1.0]])]});}
            var Q1;
            {var subQ0=sQuery(id+"F41.wireOp",EDGE,"E160");Q1=makeQuery(id+"F41.imprint","IMPRINT",FACE,{"disambiguationData":[TD([[makeQuery(id+"F41.imprint","IMPRINT",EDGE,{"derivedFrom":subQ0}),1.0]])]});}
            extrude(context, id + "F42", {"entities" : qUnion([Q0, Q1]), "operationType" : NewBodyOperationType.REMOVE, "oppositeDirection" : true, "depth" : 95 * mm});
        }
        {
            var Q0;
            Q0=makeQuery(id+"F39.opExtrude","CAP_FACE",FACE,{"disambiguationData":[OSD([sQuery(id+"F38.wireOp",EDGE,"E144"),sQuery(id+"F38.wireOp",EDGE,"E145"),sQuery(id+"F38.wireOp",EDGE,"E147"),sQuery(id+"F38.wireOp",EDGE,"E149"),sQuery(id+"F38.wireOp",EDGE,"E150"),sQuery(id+"F38.wireOp",EDGE,"E151")])],"isStart":false});
            var sketch = newSketch(context, id + "F43", { "sketchPlane" : qUnion([Q0])});
            skLineSegment(sketch, "E163.0", {"start": v(0, 0) * mm, "end": v(-86, 0) * mm});
            skLineSegment(sketch, "E164.0", {"start": v(-86, 0) * mm, "end": v(-86, 12) * mm});
            skLineSegment(sketch, "E165.0", {"start": v(0, 12) * mm, "end": v(0, 0) * mm});
            skLineSegment(sketch, "E166", {"start": v(-86, 12) * mm, "end": v(0, 12) * mm});
            skSolve(sketch);
        }
        {
            var Q0;
            Q0 = qSketchRegion(id + "F43", true);
            extrude(context, id + "F44", {"entities" : qUnion([Q0]), "operationType" : NewBodyOperationType.ADD, "depth" : 26 * mm});
        }
        {
            var Q0;
            Q0=makeQuery(id+"F39.opExtrude","CAP_FACE",FACE,{"disambiguationData":[OSD([sQuery(id+"F38.wireOp",EDGE,"E144"),sQuery(id+"F38.wireOp",EDGE,"E145"),sQuery(id+"F38.wireOp",EDGE,"E147"),sQuery(id+"F38.wireOp",EDGE,"E149"),sQuery(id+"F38.wireOp",EDGE,"E150"),sQuery(id+"F38.wireOp",EDGE,"E151")])],"isStart":true});
            var sketch = newSketch(context, id + "F45", { "sketchPlane" : qUnion([Q0])});
            skLineSegment(sketch, "E167.0", {"start": v(0, 0) * mm, "end": v(86, 0) * mm});
            skLineSegment(sketch, "E168.0", {"start": v(86, 0) * mm, "end": v(86, 12) * mm});
            skLineSegment(sketch, "E169.0", {"start": v(0, 12) * mm, "end": v(0, 0) * mm});
            skLineSegment(sketch, "E170", {"start": v(0, 12) * mm, "end": v(86, 12) * mm});
            skSolve(sketch);
        }
        {
            var Q0;
            Q0 = qSketchRegion(id + "F45", true);
            extrude(context, id + "F46", {"entities" : qUnion([Q0]), "operationType" : NewBodyOperationType.ADD, "depth" : 26 * mm});
        }
        {
            var Q0;
            Q0=makeQuery(id+"F39.opExtrude","CAP_FACE",FACE,{"disambiguationData":[OSD([sQuery(id+"F38.wireOp",EDGE,"E144"),sQuery(id+"F38.wireOp",EDGE,"E145"),sQuery(id+"F38.wireOp",EDGE,"E147"),sQuery(id+"F38.wireOp",EDGE,"E149"),sQuery(id+"F38.wireOp",EDGE,"E150"),sQuery(id+"F38.wireOp",EDGE,"E151")])],"isStart":true});
            var sketch = newSketch(context, id + "F47", { "sketchPlane" : qUnion([Q0])});
            skLineSegment(sketch, "E171.0", {"start": v(109, 57.5) * mm, "end": v(43.2, 103) * mm});
            skLineSegment(sketch, "E172", {"start": v(43.2, 103) * mm, "end": v(36.77, 89.45) * mm});
            skPoint(sketch, "E173", {"position": v(56, 12) * mm});
            skPoint(sketch, "E174", {"position": v(56, 38) * mm});
            skPoint(sketch, "E175", {"position": v(49.57, 64.55) * mm});
            skLineSegment(sketch, "E176", {"start": v(49.57, 64.55) * mm, "end": v(56, 38) * mm});
            skLineSegment(sketch, "E177", {"start": v(56, 12) * mm, "end": v(56, 38) * mm});
            skLineSegment(sketch, "E178", {"start": v(49.57, 64.55) * mm, "end": v(36.57, 64.55) * mm});
            skLineSegment(sketch, "E179", {"start": v(36.57, 64.55) * mm, "end": v(36.77, 89.45) * mm});
            skLineSegment(sketch, "E180.0", {"start": v(0, 0) * mm, "end": v(86, 0) * mm});
            skLineSegment(sketch, "E181.0", {"start": v(43.2, 103) * mm, "end": v(0, 12) * mm});
            skLineSegment(sketch, "E182", {"start": v(56, 12) * mm, "end": v(56, 0) * mm});
            skLineSegment(sketch, "E183", {"start": v(0, 12) * mm, "end": v(0, 0) * mm});
            skSolve(sketch);
        }
        {
            var Q0;
            Q0 = qSketchRegion(id + "F47", true);
            extrude(context, id + "F48", {"entities" : qUnion([Q0]), "operationType" : NewBodyOperationType.REMOVE, "endBound" : BoundingType.SYMMETRIC, "oppositeDirection" : true, "depth" : 60 * mm});
        }
        {
            var Q0;
            Q0=makeQuery(id+"F39.opExtrude","CAP_FACE",FACE,{"disambiguationData":[OSD([sQuery(id+"F38.wireOp",EDGE,"E144"),sQuery(id+"F38.wireOp",EDGE,"E145"),sQuery(id+"F38.wireOp",EDGE,"E147"),sQuery(id+"F38.wireOp",EDGE,"E149"),sQuery(id+"F38.wireOp",EDGE,"E150"),sQuery(id+"F38.wireOp",EDGE,"E151")])],"isStart":true});
            var sketch = newSketch(context, id + "F49", { "sketchPlane" : qUnion([Q0])});
            skPoint(sketch, "E184", {"position": v(58, 92.76) * mm});
            skLineSegment(sketch, "E185", {"start": v(58, 92.76) * mm, "end": v(47.2, 77.13) * mm});
            skCircle(sketch, "E186", {"center": v(47.2, 77.13) * mm, "radius": 12 * mm});
            skCircle(sketch, "E187", {"center": v(47.2, 77.13) * mm, "radius": 5 * mm});
            skSolve(sketch);
        }
        {
            var Q0;
            Q0=makeQuery(id+"F49.imprint","IMPRINT",FACE,{"disambiguationData":[TD([[makeQuery(id+"F49.imprint","IMPRINT",EDGE,{"derivedFrom":sQuery(id+"F49.wireOp",EDGE,"E187")}),1.0]])]});
            extrude(context, id + "F50", {"entities" : qUnion([Q0]), "operationType" : NewBodyOperationType.REMOVE, "oppositeDirection" : true, "depth" : 8 * mm});
        }
        {
            var Q0;
            Q0=makeQuery(id+"F48.boolean.opBoolean","COPY",EDGE,{"derivedFrom":makeQuery(id+"F48.opExtrude","SWEPT_EDGE",EDGE,{"disambiguationData":[OSD([sQuery(id+"F47.wireOp",EDGE,"E178"),sQuery(id+"F47.wireOp",EDGE,"E179")])]})});
            var Q1;
            Q1=makeQuery(id+"F48.boolean.opBoolean","COPY",EDGE,{"derivedFrom":makeQuery(id+"F48.opExtrude","SWEPT_EDGE",EDGE,{"disambiguationData":[OSD([sQuery(id+"F47.wireOp",EDGE,"E176"),sQuery(id+"F47.wireOp",EDGE,"E178")])]})});
            var Q2;
            Q2=makeQuery(id+"F48.boolean.opBoolean","COPY",EDGE,{"derivedFrom":makeQuery(id+"F48.opExtrude","SWEPT_EDGE",EDGE,{"disambiguationData":[OSD([sQuery(id+"F47.wireOp",EDGE,"E176"),sQuery(id+"F47.wireOp",EDGE,"E177")])]})});
            fillet(context, id + "F51", {"entities" : qUnion([Q0, Q1, Q2]), "radius" : 5 * mm, "tangentPropagation" : true, "allowEdgeOverflow" : false});
        }
        {
            var Q0;
            Q0=makeQuery(id+"F44.opExtrude","SWEPT_FACE",FACE,{"disambiguationData":[OSD([sQuery(id+"F43.wireOp",EDGE,"E166")])]});
            var sketch = newSketch(context, id + "F52", { "sketchPlane" : qUnion([Q0])});
            skPoint(sketch, "E188", {"position": v(-13.5, -146.5) * mm});
            skPoint(sketch, "E189", {"position": v(-73.5, -146.5) * mm});
            skCircle(sketch, "E190", {"center": v(-73.5, -146.5) * mm, "radius": 5.5 * mm});
            skCircle(sketch, "E191", {"center": v(-13.5, -146.5) * mm, "radius": 5.5 * mm});
            skSolve(sketch);
        }
        {
            var Q0;
            Q0 = qSketchRegion(id + "F52", true);
            extrude(context, id + "F53", {"entities" : qUnion([Q0]), "operationType" : NewBodyOperationType.REMOVE, "oppositeDirection" : true, "depth" : 12 * mm});
        }
        {
            var Q0;
            Q0=makeQuery(id+"F44.opExtrude","CAP_EDGE",EDGE,{"disambiguationData":[OSD([sQuery(id+"F43.wireOp",EDGE,"E164.0")])],"isStart":false});
            var Q1;
            Q1=makeQuery(id+"F44.opExtrude","CAP_EDGE",EDGE,{"disambiguationData":[OSD([sQuery(id+"F43.wireOp",EDGE,"E165.0")])],"isStart":false});
            var Q2;
            Q2=makeQuery(id+"F46.opExtrude","CAP_EDGE",EDGE,{"disambiguationData":[OSD([sQuery(id+"F45.wireOp",EDGE,"E168.0")])],"isStart":false});
            var Q3;
            Q3=makeQuery(id+"F48.boolean.opBoolean","INTERSECT",EDGE,{"derivedFrom":[makeQuery(id+"F46.opExtrude","CAP_FACE",FACE,{"disambiguationData":[OSD([sQuery(id+"F45.wireOp",EDGE,"E167.0"),sQuery(id+"F45.wireOp",EDGE,"E168.0"),sQuery(id+"F45.wireOp",EDGE,"E169.0"),sQuery(id+"F45.wireOp",EDGE,"E170")])],"isStart":false}),makeQuery(id+"F48.opExtrude","SWEPT_FACE",FACE,{"disambiguationData":[OSD([sQuery(id+"F47.wireOp",EDGE,"E177"),sQuery(id+"F47.wireOp",EDGE,"E182")])]})]});
            fillet(context, id + "F54", {"entities" : qUnion([Q0, Q1, Q2, Q3]), "radius" : 5 * mm, "tangentPropagation" : true, "allowEdgeOverflow" : false});
        }
        {
            var Q0;
            Q0=makeQuery(id+"F46.opExtrude","SWEPT_FACE",FACE,{"disambiguationData":[OSD([sQuery(id+"F45.wireOp",EDGE,"E170")])]});
            var sketch = newSketch(context, id + "F55", { "sketchPlane" : qUnion([Q0])});
            skPoint(sketch, "E192", {"position": v(-69, -58) * mm});
            skCircle(sketch, "E193", {"center": v(-69, -58) * mm, "radius": 5.5 * mm});
            skSolve(sketch);
        }
        {
            var Q0;
            Q0 = qSketchRegion(id + "F55", true);
            extrude(context, id + "F56", {"entities" : qUnion([Q0]), "operationType" : NewBodyOperationType.REMOVE, "oppositeDirection" : true, "depth" : 25 * mm});
        }
    });
